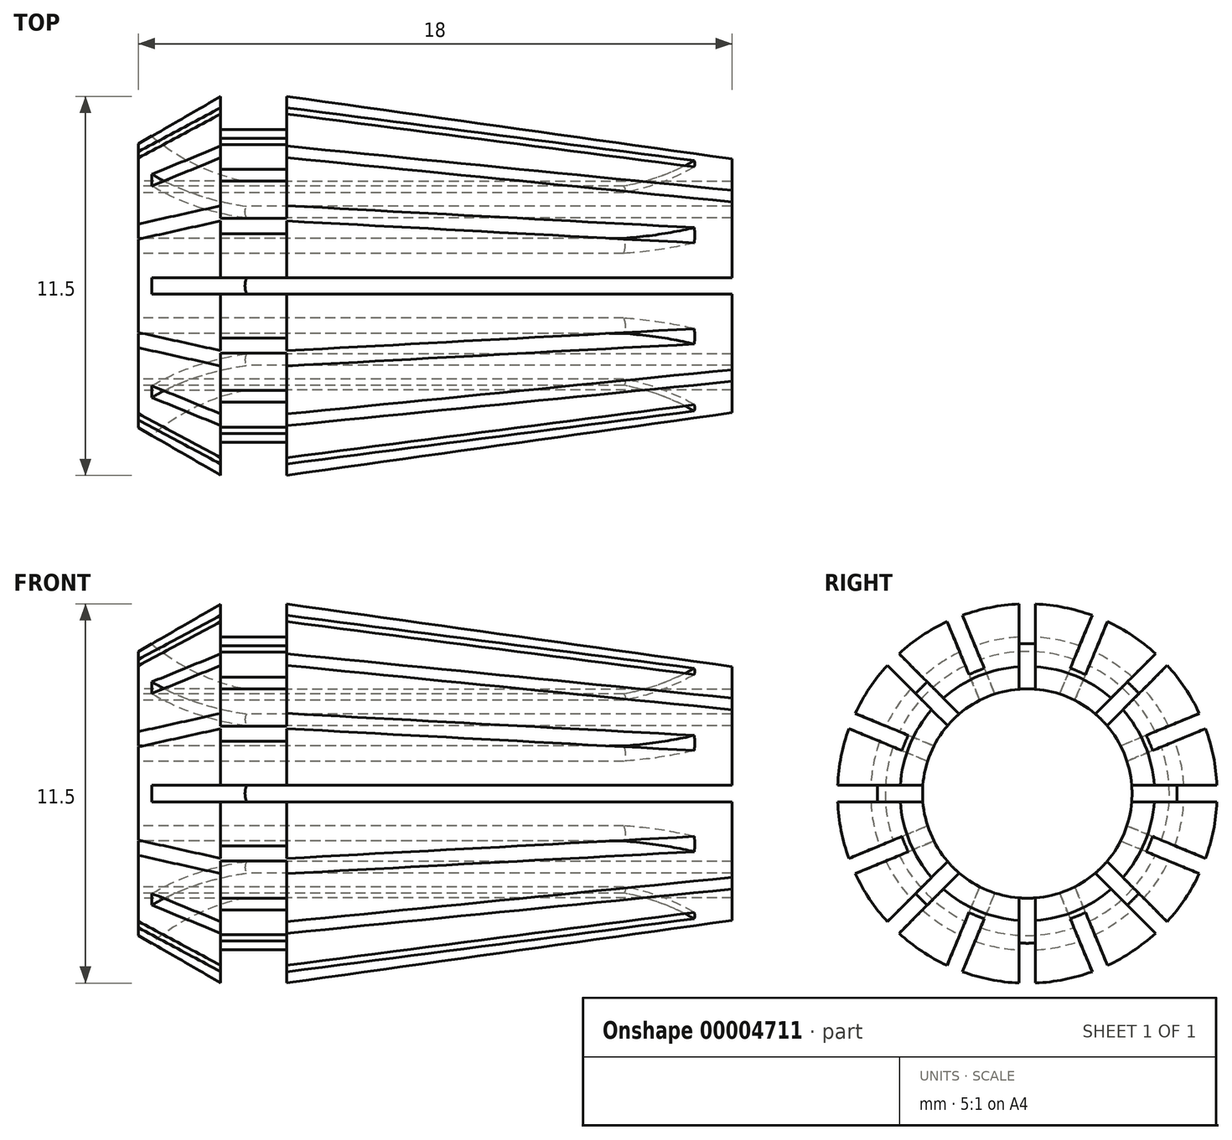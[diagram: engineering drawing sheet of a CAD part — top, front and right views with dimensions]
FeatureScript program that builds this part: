
annotation { "Feature Type Name" : "Feature", "Feature Type Description" : "" }
export const myFeature = defineFeature(function(context is Context, id is Id, definition is map)
    precondition{}
    {
        {
            var Q0;
            Q0=qCreatedBy(makeId("Front.planeOp"),FACE);
            var sketch = newSketch(context, id + "F0", { "sketchPlane" : qUnion([Q0])});
            skLineSegment(sketch, "E0.bottom", {"start": v(-18, 4.3) * mm, "end": v(-15.5, 5.75) * mm});
            skLineSegment(sketch, "E0.top", {"start": v(-18, -4.3) * mm, "end": v(-15.5, -5.75) * mm});
            skLineSegment(sketch, "E0.left", {"start": v(-18, 4.3) * mm, "end": v(-18, -4.3) * mm});
            skLineSegment(sketch, "E1", {"start": v(-15.5, 5.75) * mm, "end": v(-15.5, 4.75) * mm});
            skLineSegment(sketch, "E2", {"start": v(-15.5, -5.75) * mm, "end": v(-15.5, -4.75) * mm});
            skLineSegment(sketch, "E3", {"start": v(-15.5, 4.75) * mm, "end": v(-13.5, 4.75) * mm});
            skLineSegment(sketch, "E4", {"start": v(-13.5, 4.75) * mm, "end": v(-13.5, 5.75) * mm});
            skLineSegment(sketch, "E5", {"start": v(-13.5, 5.75) * mm, "end": v(0, 3.86) * mm});
            skLineSegment(sketch, "E6", {"start": v(-15.5, -4.75) * mm, "end": v(-13.5, -4.75) * mm});
            skLineSegment(sketch, "E7", {"start": v(-13.5, -5.75) * mm, "end": v(0, -3.86) * mm});
            skLineSegment(sketch, "E8", {"start": v(-13.5, -4.75) * mm, "end": v(-13.5, -5.75) * mm});
            skLineSegment(sketch, "E9", {"start": v(-18, 0) * mm, "end": v(0, 0) * mm});
            skLineSegment(sketch, "E10", {"start": v(-11.7, 5.5) * mm, "end": v(-11.7, -5.5) * mm, "construction": true});
            skLineSegment(sketch, "E11", {"start": v(0, 3.86) * mm, "end": v(0, 0) * mm});
            skLineSegment(sketch, "E12", {"start": v(0, -3.86) * mm, "end": v(0, 0) * mm});
            skLineSegment(sketch, "E13", {"start": v(0, 0) * mm, "end": v(27.43, 0) * mm, "construction": true});
            skLineSegment(sketch, "E14", {"start": v(27.43, 0) * mm, "end": v(0, 3.86) * mm, "construction": true});
            skSolve(sketch);
        }
        {
            var Q0;
            {var subQ1=sQuery(id+"F0.wireOp",EDGE,"E0.bottom");Q0=makeQuery(id+"F0.imprint","IMPRINT",FACE,{"disambiguationData":[TD([[makeQuery(id+"F0.imprint","IMPRINT",EDGE,{"derivedFrom":subQ1}),-1.0]])]});}
            var Q1;
            Q1=sQuery(id+"F0.wireOp",EDGE,"E9");
            revolve(context, id + "F1", {"entities" : qUnion([Q0]), "axis" : qUnion([Q1]), "revolveType" : RevolveType.FULL});
        }
        {
            var Q0;
            Q0=makeQuery(id+"F1.opRevolve","SWEPT_FACE",FACE,{"disambiguationData":[OSD([sQuery(id+"F0.wireOp",EDGE,"E0.left")])]});
            var sketch = newSketch(context, id + "F2", { "sketchPlane" : qUnion([Q0])});
            skCircle(sketch, "E15", {"center": v(0, 0) * mm, "radius": 3.18 * mm});
            skSolve(sketch);
        }
        {
            var Q0;
            Q0=makeQuery(id+"F2.imprint","IMPRINT",FACE,{"disambiguationData":[TD([[makeQuery(id+"F2.imprint","IMPRINT",EDGE,{"derivedFrom":sQuery(id+"F2.wireOp",EDGE,"E15")}),1.0]])]});
            extrude(context, id + "F3", {"entities" : qUnion([Q0]), "operationType" : NewBodyOperationType.REMOVE, "oppositeDirection" : true, "depth" : 25.4 * mm});
        }
        {
            var Q0;
            Q0=qCreatedBy(makeId("Front.planeOp"),FACE);
            var sketch = newSketch(context, id + "F4", { "sketchPlane" : qUnion([Q0])});
            skArc(sketch, "E16", {"start": v(-19.19, 6.57) * mm, "mid": v(-16.85, 4) * mm, "end": v(-13.5, 3.05) * mm});
            skLineSegment(sketch, "E17", {"start": v(0, 0) * mm, "end": v(-18, 0) * mm, "construction": true});
            skLineSegment(sketch, "E18.0", {"start": v(-19.8, 3.05) * mm, "end": v(-29.94, 3.05) * mm, "construction": true});
            skLineSegment(sketch, "E19.0", {"start": v(-13.5, 7.43) * mm, "end": v(-13.5, 0) * mm, "construction": true});
            skLineSegment(sketch, "E20.0", {"start": v(-4.5, 7.56) * mm, "end": v(-4.5, -7.85) * mm, "construction": true});
            skLineSegment(sketch, "E21", {"start": v(-13.5, 3.05) * mm, "end": v(0.98, 3.05) * mm});
            skLineSegment(sketch, "E22", {"start": v(0.98, 3.05) * mm, "end": v(0.98, 6.57) * mm});
            skLineSegment(sketch, "E23", {"start": v(0.98, 6.57) * mm, "end": v(-19.19, 6.57) * mm});
            skPoint(sketch, "E24", {"position": v(-13.5, 3.05) * mm});
            skLineSegment(sketch, "E25", {"start": v(-9, 0) * mm, "end": v(-9, -5.39) * mm, "construction": true});
            skLineSegment(sketch, "E26.MirrorCS", {"start": v(-19.08, -3.05) * mm, "end": v(-19.08, -6.57) * mm});
            skLineSegment(sketch, "E27.MirrorCS", {"start": v(-4.5, -3.05) * mm, "end": v(-19.08, -3.05) * mm});
            skLineSegment(sketch, "E28.MirrorCS", {"start": v(-19.08, -6.57) * mm, "end": v(1.19, -6.57) * mm});
            skArc(sketch, "E29.MirrorCS", {"start": v(1.19, -6.57) * mm, "mid": v(-1.15, -4) * mm, "end": v(-4.5, -3.05) * mm});
            skSolve(sketch);
        }
        {
            var Q0;
            Q0=makeQuery(id+"F4.imprint","IMPRINT",FACE,{"disambiguationData":[TD([[makeQuery(id+"F4.imprint","IMPRINT",EDGE,{"derivedFrom":sQuery(id+"F4.wireOp",EDGE,"E16")}),1.0]])]});
            extrude(context, id + "F5", {"entities" : qUnion([Q0]), "endBound" : BoundingType.SYMMETRIC, "depth" : .5 * mm});
        }
        {
            var Q0;
            Q0=makeQuery(id+"F5.opExtrude","SWEPT_BODY",BODY,{"disambiguationData":[OSD([sQuery(id+"F4.wireOp",EDGE,"E16"),sQuery(id+"F4.wireOp",EDGE,"E21"),sQuery(id+"F4.wireOp",EDGE,"E22"),sQuery(id+"F4.wireOp",EDGE,"E23")])]});
            var Q1;
            Q1=makeQuery(id+"F3.boolean.opBoolean","COPY",FACE,{"derivedFrom":makeQuery(id+"F3.opExtrude","SWEPT_FACE",FACE,{"disambiguationData":[OSD([sQuery(id+"F2.wireOp",EDGE,"E15")])]})});
            circularPattern(context, id + "F6", {"entities" : qUnion([Q0]), "axis" : qUnion([Q1]), "angle" : 360 * degree, "instanceCount" : 8, "equalSpace" : true});
        }
        {
            var Q0;
            Q0=makeQuery(id+"F4.imprint","IMPRINT",FACE,{"disambiguationData":[TD([[makeQuery(id+"F4.imprint","IMPRINT",EDGE,{"derivedFrom":sQuery(id+"F4.wireOp",EDGE,"E26.MirrorCS")}),1.0]])]});
            extrude(context, id + "F7", {"entities" : qUnion([Q0]), "endBound" : BoundingType.SYMMETRIC, "depth" : .5 * mm});
        }
        {
            var Q0;
            Q0=makeQuery(id+"F7.opExtrude","SWEPT_BODY",BODY,{"disambiguationData":[OSD([sQuery(id+"F4.wireOp",EDGE,"E26.MirrorCS"),sQuery(id+"F4.wireOp",EDGE,"E27.MirrorCS"),sQuery(id+"F4.wireOp",EDGE,"E28.MirrorCS"),sQuery(id+"F4.wireOp",EDGE,"E29.MirrorCS")])]});
            var Q1;
            Q1=sQuery(id+"F4.wireOp",EDGE,"E17");
            transform(context, id + "F8", {"entities" : qUnion([Q0]), "transformType" : TransformType.ROTATION, "transformAxis" : qUnion([Q1]), "angle" : 22.5 * degree, "makeCopy" : false});
        }
        {
            var Q0;
            Q0=makeQuery(id+"F7.opExtrude","SWEPT_BODY",BODY,{"disambiguationData":[OSD([sQuery(id+"F4.wireOp",EDGE,"E26.MirrorCS"),sQuery(id+"F4.wireOp",EDGE,"E27.MirrorCS"),sQuery(id+"F4.wireOp",EDGE,"E28.MirrorCS"),sQuery(id+"F4.wireOp",EDGE,"E29.MirrorCS")])]});
            var Q1;
            Q1=sQuery(id+"F4.wireOp",EDGE,"E17");
            circularPattern(context, id + "F9", {"entities" : qUnion([Q0]), "axis" : qUnion([Q1]), "angle" : 360 * degree, "instanceCount" : 8, "equalSpace" : true});
        }
        {
            var Q0;
            Q0=makeQuery(id+"F5.opExtrude","SWEPT_BODY",BODY,{"disambiguationData":[OSD([sQuery(id+"F4.wireOp",EDGE,"E16"),sQuery(id+"F4.wireOp",EDGE,"E21"),sQuery(id+"F4.wireOp",EDGE,"E22"),sQuery(id+"F4.wireOp",EDGE,"E23")])]});
            var Q1;
            Q1=makeQuery(id+"F6.opPattern","COPY",BODY,{"derivedFrom":makeQuery(id+"F5.opExtrude","SWEPT_BODY",BODY,{"disambiguationData":[OSD([sQuery(id+"F4.wireOp",EDGE,"E16"),sQuery(id+"F4.wireOp",EDGE,"E21"),sQuery(id+"F4.wireOp",EDGE,"E22"),sQuery(id+"F4.wireOp",EDGE,"E23")])]}),"instanceName":"1"});
            var Q2;
            Q2=makeQuery(id+"F6.opPattern","COPY",BODY,{"derivedFrom":makeQuery(id+"F5.opExtrude","SWEPT_BODY",BODY,{"disambiguationData":[OSD([sQuery(id+"F4.wireOp",EDGE,"E16"),sQuery(id+"F4.wireOp",EDGE,"E21"),sQuery(id+"F4.wireOp",EDGE,"E22"),sQuery(id+"F4.wireOp",EDGE,"E23")])]}),"instanceName":"3"});
            var Q3;
            Q3=makeQuery(id+"F6.opPattern","COPY",BODY,{"derivedFrom":makeQuery(id+"F5.opExtrude","SWEPT_BODY",BODY,{"disambiguationData":[OSD([sQuery(id+"F4.wireOp",EDGE,"E16"),sQuery(id+"F4.wireOp",EDGE,"E21"),sQuery(id+"F4.wireOp",EDGE,"E22"),sQuery(id+"F4.wireOp",EDGE,"E23")])]}),"instanceName":"4"});
            var Q4;
            Q4=makeQuery(id+"F6.opPattern","COPY",BODY,{"derivedFrom":makeQuery(id+"F5.opExtrude","SWEPT_BODY",BODY,{"disambiguationData":[OSD([sQuery(id+"F4.wireOp",EDGE,"E16"),sQuery(id+"F4.wireOp",EDGE,"E21"),sQuery(id+"F4.wireOp",EDGE,"E22"),sQuery(id+"F4.wireOp",EDGE,"E23")])]}),"instanceName":"5"});
            var Q5;
            Q5=makeQuery(id+"F6.opPattern","COPY",BODY,{"derivedFrom":makeQuery(id+"F5.opExtrude","SWEPT_BODY",BODY,{"disambiguationData":[OSD([sQuery(id+"F4.wireOp",EDGE,"E16"),sQuery(id+"F4.wireOp",EDGE,"E21"),sQuery(id+"F4.wireOp",EDGE,"E22"),sQuery(id+"F4.wireOp",EDGE,"E23")])]}),"instanceName":"6"});
            var Q6;
            Q6=makeQuery(id+"F6.opPattern","COPY",BODY,{"derivedFrom":makeQuery(id+"F5.opExtrude","SWEPT_BODY",BODY,{"disambiguationData":[OSD([sQuery(id+"F4.wireOp",EDGE,"E16"),sQuery(id+"F4.wireOp",EDGE,"E21"),sQuery(id+"F4.wireOp",EDGE,"E22"),sQuery(id+"F4.wireOp",EDGE,"E23")])]}),"instanceName":"7"});
            var Q7;
            Q7=makeQuery(id+"F6.opPattern","COPY",BODY,{"derivedFrom":makeQuery(id+"F5.opExtrude","SWEPT_BODY",BODY,{"disambiguationData":[OSD([sQuery(id+"F4.wireOp",EDGE,"E16"),sQuery(id+"F4.wireOp",EDGE,"E21"),sQuery(id+"F4.wireOp",EDGE,"E22"),sQuery(id+"F4.wireOp",EDGE,"E23")])]}),"instanceName":"2"});
            var Q8;
            Q8=makeQuery(id+"F1.opRevolve","SWEPT_BODY",BODY,{"disambiguationData":[OSD([sQuery(id+"F0.wireOp",EDGE,"E0.bottom"),sQuery(id+"F0.wireOp",EDGE,"E0.left"),sQuery(id+"F0.wireOp",EDGE,"E1"),sQuery(id+"F0.wireOp",EDGE,"E3"),sQuery(id+"F0.wireOp",EDGE,"E4"),sQuery(id+"F0.wireOp",EDGE,"E5"),sQuery(id+"F0.wireOp",EDGE,"E9"),sQuery(id+"F0.wireOp",EDGE,"E11")])]});
            booleanBodies(context, id + "F10", {"operationType" : BooleanOperationType.SUBTRACTION, "tools" : qUnion([Q0, Q1, Q2, Q3, Q4, Q5, Q6, Q7]), "targets" : qUnion([Q8])});
        }
        {
            var Q0;
            Q0=makeQuery(id+"F9.opPattern","COPY",BODY,{"derivedFrom":makeQuery(id+"F7.opExtrude","SWEPT_BODY",BODY,{"disambiguationData":[OSD([sQuery(id+"F4.wireOp",EDGE,"E26.MirrorCS"),sQuery(id+"F4.wireOp",EDGE,"E27.MirrorCS"),sQuery(id+"F4.wireOp",EDGE,"E28.MirrorCS"),sQuery(id+"F4.wireOp",EDGE,"E29.MirrorCS")])]}),"instanceName":"4"});
            var Q1;
            Q1=makeQuery(id+"F9.opPattern","COPY",BODY,{"derivedFrom":makeQuery(id+"F7.opExtrude","SWEPT_BODY",BODY,{"disambiguationData":[OSD([sQuery(id+"F4.wireOp",EDGE,"E26.MirrorCS"),sQuery(id+"F4.wireOp",EDGE,"E27.MirrorCS"),sQuery(id+"F4.wireOp",EDGE,"E28.MirrorCS"),sQuery(id+"F4.wireOp",EDGE,"E29.MirrorCS")])]}),"instanceName":"3"});
            var Q2;
            Q2=makeQuery(id+"F9.opPattern","COPY",BODY,{"derivedFrom":makeQuery(id+"F7.opExtrude","SWEPT_BODY",BODY,{"disambiguationData":[OSD([sQuery(id+"F4.wireOp",EDGE,"E26.MirrorCS"),sQuery(id+"F4.wireOp",EDGE,"E27.MirrorCS"),sQuery(id+"F4.wireOp",EDGE,"E28.MirrorCS"),sQuery(id+"F4.wireOp",EDGE,"E29.MirrorCS")])]}),"instanceName":"2"});
            var Q3;
            Q3=makeQuery(id+"F9.opPattern","COPY",BODY,{"derivedFrom":makeQuery(id+"F7.opExtrude","SWEPT_BODY",BODY,{"disambiguationData":[OSD([sQuery(id+"F4.wireOp",EDGE,"E26.MirrorCS"),sQuery(id+"F4.wireOp",EDGE,"E27.MirrorCS"),sQuery(id+"F4.wireOp",EDGE,"E28.MirrorCS"),sQuery(id+"F4.wireOp",EDGE,"E29.MirrorCS")])]}),"instanceName":"1"});
            var Q4;
            Q4=makeQuery(id+"F7.opExtrude","SWEPT_BODY",BODY,{"disambiguationData":[OSD([sQuery(id+"F4.wireOp",EDGE,"E26.MirrorCS"),sQuery(id+"F4.wireOp",EDGE,"E27.MirrorCS"),sQuery(id+"F4.wireOp",EDGE,"E28.MirrorCS"),sQuery(id+"F4.wireOp",EDGE,"E29.MirrorCS")])]});
            var Q5;
            Q5=makeQuery(id+"F9.opPattern","COPY",BODY,{"derivedFrom":makeQuery(id+"F7.opExtrude","SWEPT_BODY",BODY,{"disambiguationData":[OSD([sQuery(id+"F4.wireOp",EDGE,"E26.MirrorCS"),sQuery(id+"F4.wireOp",EDGE,"E27.MirrorCS"),sQuery(id+"F4.wireOp",EDGE,"E28.MirrorCS"),sQuery(id+"F4.wireOp",EDGE,"E29.MirrorCS")])]}),"instanceName":"7"});
            var Q6;
            Q6=makeQuery(id+"F9.opPattern","COPY",BODY,{"derivedFrom":makeQuery(id+"F7.opExtrude","SWEPT_BODY",BODY,{"disambiguationData":[OSD([sQuery(id+"F4.wireOp",EDGE,"E26.MirrorCS"),sQuery(id+"F4.wireOp",EDGE,"E27.MirrorCS"),sQuery(id+"F4.wireOp",EDGE,"E28.MirrorCS"),sQuery(id+"F4.wireOp",EDGE,"E29.MirrorCS")])]}),"instanceName":"6"});
            var Q7;
            Q7=makeQuery(id+"F9.opPattern","COPY",BODY,{"derivedFrom":makeQuery(id+"F7.opExtrude","SWEPT_BODY",BODY,{"disambiguationData":[OSD([sQuery(id+"F4.wireOp",EDGE,"E26.MirrorCS"),sQuery(id+"F4.wireOp",EDGE,"E27.MirrorCS"),sQuery(id+"F4.wireOp",EDGE,"E28.MirrorCS"),sQuery(id+"F4.wireOp",EDGE,"E29.MirrorCS")])]}),"instanceName":"5"});
            var Q8;
            Q8=makeQuery(id+"F1.opRevolve","SWEPT_BODY",BODY,{"disambiguationData":[OSD([sQuery(id+"F0.wireOp",EDGE,"E0.bottom"),sQuery(id+"F0.wireOp",EDGE,"E0.left"),sQuery(id+"F0.wireOp",EDGE,"E1"),sQuery(id+"F0.wireOp",EDGE,"E3"),sQuery(id+"F0.wireOp",EDGE,"E4"),sQuery(id+"F0.wireOp",EDGE,"E5"),sQuery(id+"F0.wireOp",EDGE,"E9"),sQuery(id+"F0.wireOp",EDGE,"E11")])]});
            booleanBodies(context, id + "F11", {"operationType" : BooleanOperationType.SUBTRACTION, "tools" : qUnion([Q0, Q1, Q2, Q3, Q4, Q5, Q6, Q7]), "targets" : qUnion([Q8])});
        }
    });
